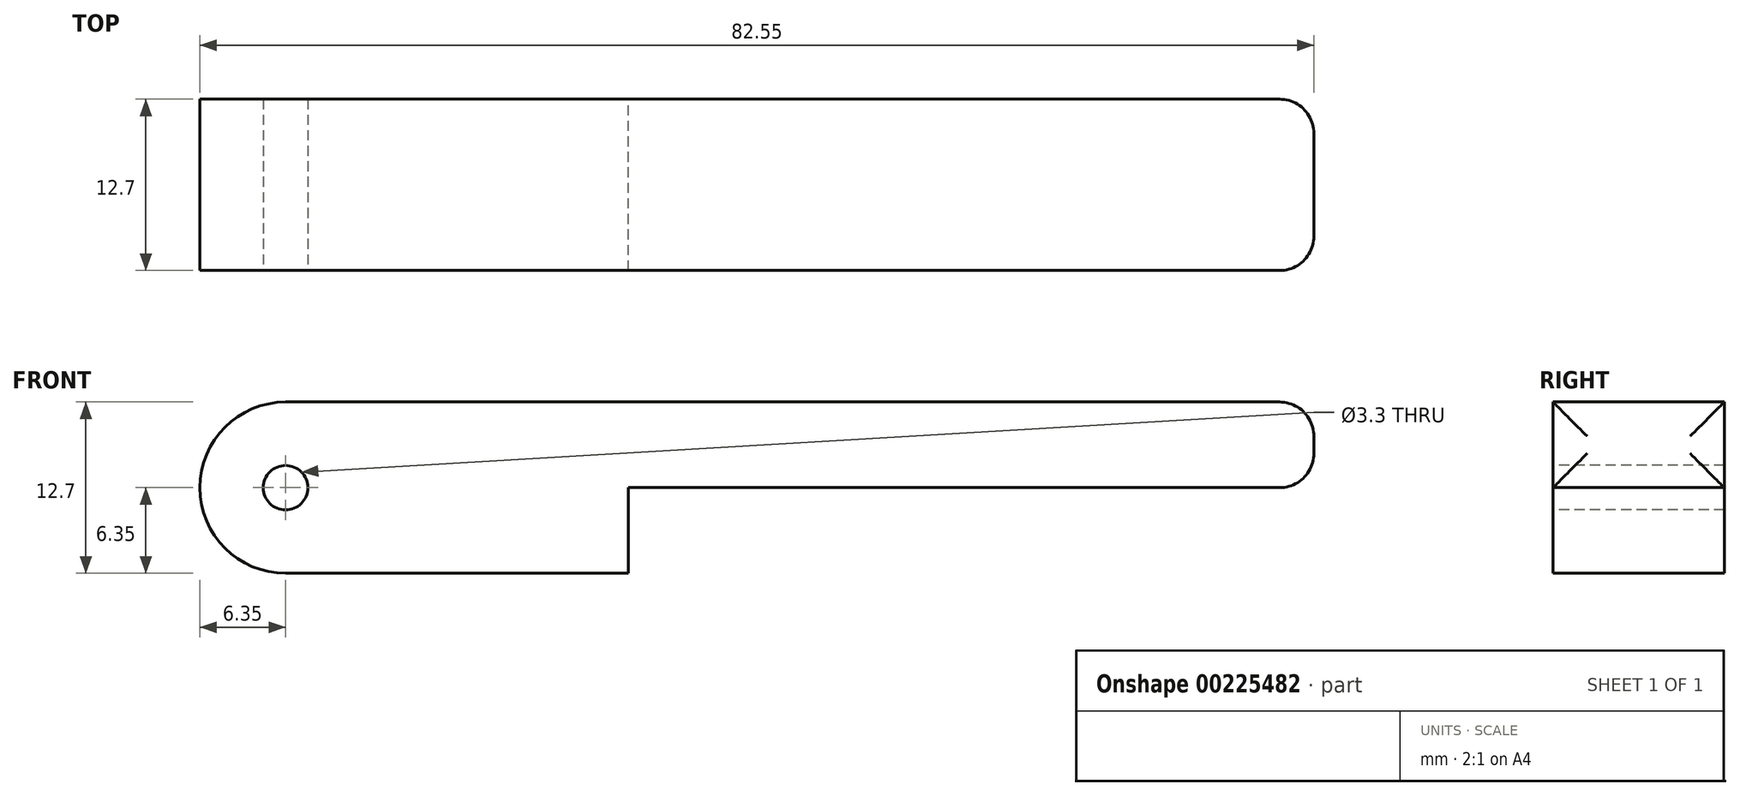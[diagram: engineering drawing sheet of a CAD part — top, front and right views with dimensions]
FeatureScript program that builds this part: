
annotation { "Feature Type Name" : "Feature", "Feature Type Description" : "" }
export const myFeature = defineFeature(function(context is Context, id is Id, definition is map)
    precondition{}
    {
        {
            var Q0;
            Q0=qCreatedBy(makeId("Front.planeOp"),FACE);
            var sketch = newSketch(context, id + "F0", { "sketchPlane" : qUnion([Q0])});
            skLineSegment(sketch, "E0.bottom", {"start": v(0, 0) * mm, "end": v(25.4, 0) * mm});
            skLineSegment(sketch, "E0.top", {"start": v(0, 12.7) * mm, "end": v(19.05, 12.7) * mm});
            skArc(sketch, "E1", {"start": v(0, 12.7) * mm, "mid": v(-6.35, 6.35) * mm, "end": v(0, 0) * mm});
            skLineSegment(sketch, "E2", {"start": v(25.4, 0) * mm, "end": v(25.4, 6.35) * mm});
            skLineSegment(sketch, "E3", {"start": v(25.4, 6.35) * mm, "end": v(76.2, 6.35) * mm});
            skLineSegment(sketch, "E4", {"start": v(76.2, 6.35) * mm, "end": v(76.2, 12.7) * mm});
            skLineSegment(sketch, "E5", {"start": v(19.05, 12.7) * mm, "end": v(76.2, 12.7) * mm});
            skSolve(sketch);
        }
        {
            var Q0;
            Q0=makeQuery(id+"F0.imprint","IMPRINT",FACE,{"disambiguationData":[TD([[makeQuery(id+"F0.imprint","IMPRINT",EDGE,{"derivedFrom":sQuery(id+"F0.wireOp",EDGE,"E0.bottom")}),1.0]])]});
            extrude(context, id + "F1", {"entities" : qUnion([Q0]), "depth" : 12.7 * mm});
        }
        {
            var Q0;
            Q0=makeQuery(id+"F1.opExtrude","CAP_FACE",FACE,{"disambiguationData":[OSD([sQuery(id+"F0.wireOp",EDGE,"E0.bottom"),sQuery(id+"F0.wireOp",EDGE,"E0.top"),sQuery(id+"F0.wireOp",EDGE,"E1"),sQuery(id+"F0.wireOp",EDGE,"E2"),sQuery(id+"F0.wireOp",EDGE,"E3"),sQuery(id+"F0.wireOp",EDGE,"E4"),sQuery(id+"F0.wireOp",EDGE,"E5")])],"isStart":false});
            var sketch = newSketch(context, id + "F2", { "sketchPlane" : qUnion([Q0])});
            skPoint(sketch, "E6", {"position": v(0, 6.35) * mm});
            skSolve(sketch);
        }
        {
            var Q0;
            Q0=sQuery(id+"F2.wireOp",VERTEX,"E6");
            var Q1;
            Q1=makeQuery(id+"F1.opExtrude","SWEPT_BODY",BODY,{"disambiguationData":[OSD([sQuery(id+"F0.wireOp",EDGE,"E0.bottom"),sQuery(id+"F0.wireOp",EDGE,"E0.top"),sQuery(id+"F0.wireOp",EDGE,"E1"),sQuery(id+"F0.wireOp",EDGE,"E2"),sQuery(id+"F0.wireOp",EDGE,"E3"),sQuery(id+"F0.wireOp",EDGE,"E4"),sQuery(id+"F0.wireOp",EDGE,"E5")])]});
            hole(context, id + "F3", {"style" : HoleStyle.C_BORE, "endStyle" : HoleEndStyle.THROUGH, "holeDiameter" : 3.3 * mm, "cBoreDiameter" : 6.5 * mm, "cBoreDepth" : 0 * mm, "startFromSketch" : true, "locations" : qUnion([Q0]), "scope" : qUnion([Q1]), "isTappedThrough" : true});
        }
        {
            var Q0;
            Q0=makeQuery(id+"F1.opExtrude","CAP_EDGE",EDGE,{"disambiguationData":[OSD([sQuery(id+"F0.wireOp",EDGE,"E4")])],"isStart":false});
            var Q1;
            Q1=makeQuery(id+"F1.opExtrude","SWEPT_FACE",FACE,{"disambiguationData":[OSD([sQuery(id+"F0.wireOp",EDGE,"E4")])]});
            fillet(context, id + "F4", {"entities" : qUnion([Q0, Q1]), "radius" : 2.54 * mm, "tangentPropagation" : true, "allowEdgeOverflow" : false});
        }
    });
